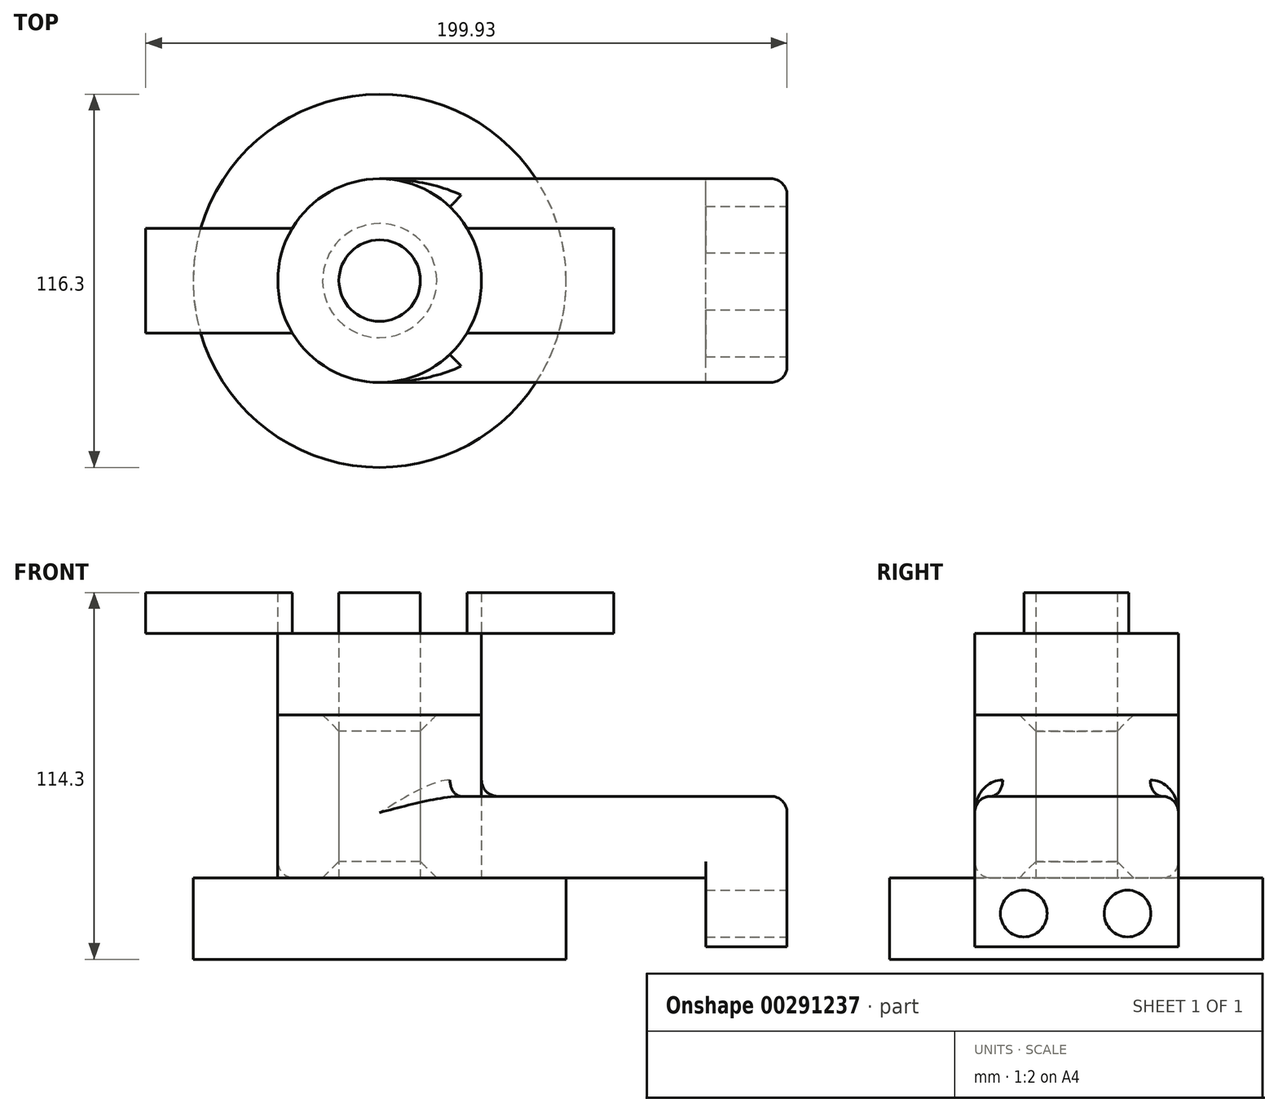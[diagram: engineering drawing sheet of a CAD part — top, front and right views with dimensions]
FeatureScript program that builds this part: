
annotation { "Feature Type Name" : "Feature", "Feature Type Description" : "" }
export const myFeature = defineFeature(function(context is Context, id is Id, definition is map)
    precondition{}
    {
        {
            var Q0;
            Q0=qCreatedBy(makeId("Top.planeOp"),FACE);
            var sketch = newSketch(context, id + "F0", { "sketchPlane" : qUnion([Q0])});
            skLineSegment(sketch, "E0.bottom", {"start": v(0, 0) * mm, "end": v(127, 0) * mm});
            skLineSegment(sketch, "E0.top", {"start": v(0, 63.5) * mm, "end": v(127, 63.5) * mm});
            skLineSegment(sketch, "E0.left", {"start": v(0, 0) * mm, "end": v(0, 63.5) * mm});
            skLineSegment(sketch, "E0.right", {"start": v(127, 0) * mm, "end": v(127, 63.5) * mm});
            skCircle(sketch, "E1", {"center": v(0, 31.75) * mm, "radius": 31.75 * mm});
            skCircle(sketch, "E2", {"center": v(0, 31.75) * mm, "radius": 12.7 * mm});
            skSolve(sketch);
        }
        {
            var Q0;
            {var subQ1=sQuery(id+"F0.wireOp",EDGE,"E0.left");var subQ3=sQuery(id+"F0.wireOp",EDGE,"E2");var subQ4=makeQuery(id+"F0.imprint","INTERSECT",VERTEX,{"disambiguationData":[OD(0.0)],"derivedFrom":[subQ1,subQ3]});Q0=makeQuery(id+"F0.imprint","IMPRINT",FACE,{"disambiguationData":[TD([[makeQuery(id+"F0.imprint","IMPRINT",EDGE,{"disambiguationData":[TD([[subQ4,1.0]])],"derivedFrom":subQ3}),-1.0]])]});}
            var Q1;
            {var subQ1=sQuery(id+"F0.wireOp",EDGE,"E0.left");var subQ3=sQuery(id+"F0.wireOp",EDGE,"E2");var subQ4=makeQuery(id+"F0.imprint","INTERSECT",VERTEX,{"disambiguationData":[OD(0.0)],"derivedFrom":[subQ1,subQ3]});Q1=makeQuery(id+"F0.imprint","IMPRINT",FACE,{"disambiguationData":[TD([[makeQuery(id+"F0.imprint","IMPRINT",EDGE,{"disambiguationData":[TD([[subQ4,-1.0]])],"derivedFrom":subQ3}),-1.0]])]});}
            var Q2;
            {var subQ0=sQuery(id+"F0.wireOp",EDGE,"E0.bottom");Q2=makeQuery(id+"F0.imprint","IMPRINT",FACE,{"disambiguationData":[TD([[makeQuery(id+"F0.imprint","IMPRINT",EDGE,{"derivedFrom":subQ0}),1.0]])]});}
            extrude(context, id + "F1", {"entities" : qUnion([Q0, Q1, Q2]), "depth" : 25.4 * mm});
        }
        {
            var Q0;
            {var subQ1=sQuery(id+"F0.wireOp",EDGE,"E0.left");var subQ3=sQuery(id+"F0.wireOp",EDGE,"E2");var subQ4=makeQuery(id+"F0.imprint","INTERSECT",VERTEX,{"disambiguationData":[OD(0.0)],"derivedFrom":[subQ1,subQ3]});Q0=makeQuery(id+"F0.imprint","IMPRINT",FACE,{"disambiguationData":[TD([[makeQuery(id+"F0.imprint","IMPRINT",EDGE,{"disambiguationData":[TD([[subQ4,1.0]])],"derivedFrom":subQ3}),-1.0]])]});}
            var Q1;
            {var subQ1=sQuery(id+"F0.wireOp",EDGE,"E0.left");var subQ3=sQuery(id+"F0.wireOp",EDGE,"E2");var subQ4=makeQuery(id+"F0.imprint","INTERSECT",VERTEX,{"disambiguationData":[OD(0.0)],"derivedFrom":[subQ1,subQ3]});Q1=makeQuery(id+"F0.imprint","IMPRINT",FACE,{"disambiguationData":[TD([[makeQuery(id+"F0.imprint","IMPRINT",EDGE,{"disambiguationData":[TD([[subQ4,-1.0]])],"derivedFrom":subQ3}),-1.0]])]});}
            extrude(context, id + "F2", {"entities" : qUnion([Q0, Q1]), "operationType" : NewBodyOperationType.ADD, "depth" : 50.8 * mm});
        }
        {
            var Q0;
            Q0=makeQuery(id+"F1.opExtrude","SWEPT_FACE",FACE,{"disambiguationData":[OSD([sQuery(id+"F0.wireOp",EDGE,"E0.right")])]});
            var sketch = newSketch(context, id + "F3", { "sketchPlane" : qUnion([Q0])});
            skLineSegment(sketch, "E3.bottom", {"start": v(0, 0) * mm, "end": v(63.5, 0) * mm});
            skLineSegment(sketch, "E3.top", {"start": v(0, -21.55) * mm, "end": v(63.5, -21.55) * mm});
            skLineSegment(sketch, "E3.left", {"start": v(0, 0) * mm, "end": v(0, -21.55) * mm});
            skLineSegment(sketch, "E3.right", {"start": v(63.5, 0) * mm, "end": v(63.5, -21.55) * mm});
            skSolve(sketch);
        }
        {
            var Q0;
            Q0=makeQuery(id+"F3.imprint","IMPRINT",FACE,{"disambiguationData":[TD([[makeQuery(id+"F3.imprint","IMPRINT",EDGE,{"derivedFrom":sQuery(id+"F3.wireOp",EDGE,"E3.bottom")}),-1.0]])]});
            var sketch = newSketch(context, id + "F4", { "sketchPlane" : qUnion([Q0])});
            skLineSegment(sketch, "E4", {"start": v(31.5, 0) * mm, "end": v(31.5, -22.54) * mm, "construction": true});
            skCircle(sketch, "E5", {"center": v(15.33, -11.15) * mm, "radius": 7.27 * mm});
            skCircle(sketch, "E6.MirrorC", {"center": v(47.68, -11.15) * mm, "radius": 7.27 * mm});
            skSolve(sketch);
        }
        {
            var Q0;
            Q0=makeQuery(id+"F4.imprint","IMPRINT",FACE,{"disambiguationData":[TD([[makeQuery(id+"F4.imprint","IMPRINT",EDGE,{"derivedFrom":sQuery(id+"F4.wireOp",EDGE,"E5")}),-1.0]])]});
            extrude(context, id + "F5", {"entities" : qUnion([Q0]), "operationType" : NewBodyOperationType.ADD, "oppositeDirection" : true, "depth" : 25.4 * mm});
        }
        {
            var Q0;
            {var subQ0=sQuery(id+"F0.wireOp",EDGE,"E1");Q0=makeQuery(id+"F2.boolean.opBoolean","INTERSECT",EDGE,{"derivedFrom":[makeQuery(id+"F1.opExtrude","CAP_FACE",FACE,{"disambiguationData":[OSD([sQuery(id+"F0.wireOp",EDGE,"E0.bottom"),sQuery(id+"F0.wireOp",EDGE,"E0.top"),sQuery(id+"F0.wireOp",EDGE,"E0.right"),subQ0,sQuery(id+"F0.wireOp",EDGE,"E2")])],"isStart":false}),makeQuery(id+"F2.opExtrude","SWEPT_FACE",FACE,{"disambiguationData":[OSD([subQ0])]})]});}
            var Q1;
            Q1=makeQuery(id+"F1.opExtrude","CAP_EDGE",EDGE,{"disambiguationData":[OSD([sQuery(id+"F0.wireOp",EDGE,"E0.bottom")])],"isStart":false});
            var Q2;
            Q2=makeQuery(id+"F1.opExtrude","CAP_EDGE",EDGE,{"disambiguationData":[OSD([sQuery(id+"F0.wireOp",EDGE,"E0.top")])],"isStart":false});
            var Q3;
            Q3=makeQuery(id+"F1.opExtrude","CAP_EDGE",EDGE,{"disambiguationData":[OSD([sQuery(id+"F0.wireOp",EDGE,"E0.right")])],"isStart":false});
            var Q4;
            Q4=makeQuery(id+"F1.opExtrude","CAP_EDGE",EDGE,{"disambiguationData":[OSD([sQuery(id+"F0.wireOp",EDGE,"E0.bottom")])],"isStart":true});
            var Q5;
            Q5=makeQuery(id+"F5.opExtrude","CAP_EDGE",EDGE,{"disambiguationData":[OSD([sQuery(id+"F3.wireOp",EDGE,"E3.bottom")])],"isStart":false});
            fillet(context, id + "F6", {"entities" : qUnion([Q0, Q1, Q2, Q3, Q4, Q5]), "radius" : 5.08 * mm, "tangentPropagation" : true, "allowEdgeOverflow" : false});
        }
        {
            var Q0;
            Q0=makeQuery(id+"F2.opExtrude","CAP_EDGE",EDGE,{"disambiguationData":[OSD([sQuery(id+"F0.wireOp",EDGE,"E2")])],"isStart":false});
            var Q1;
            Q1=makeQuery(id+"F1.opExtrude","CAP_EDGE",EDGE,{"disambiguationData":[OSD([sQuery(id+"F0.wireOp",EDGE,"E2")])],"isStart":true});
            chamfer(context, id + "F7", {"entities" : qUnion([Q0, Q1]), "width" : 5.08 * mm, "tangentPropagation" : true});
        }
        {
            var Q0;
            Q0=makeQuery(id+"F5.boolean.opBoolean","MERGE",EDGE,{"derivedFrom":[makeQuery(id+"F1.opExtrude","SWEPT_EDGE",EDGE,{"disambiguationData":[OSD([sQuery(id+"F0.wireOp",EDGE,"E0.bottom"),sQuery(id+"F0.wireOp",EDGE,"E0.right")])]}),makeQuery(id+"F5.opExtrude","CAP_EDGE",EDGE,{"disambiguationData":[OSD([sQuery(id+"F3.wireOp",EDGE,"E3.left")])],"isStart":true})]});
            var Q1;
            Q1=makeQuery(id+"F5.boolean.opBoolean","MERGE",EDGE,{"derivedFrom":[makeQuery(id+"F1.opExtrude","SWEPT_EDGE",EDGE,{"disambiguationData":[OSD([sQuery(id+"F0.wireOp",EDGE,"E0.top"),sQuery(id+"F0.wireOp",EDGE,"E0.right")])]}),makeQuery(id+"F5.opExtrude","CAP_EDGE",EDGE,{"disambiguationData":[OSD([sQuery(id+"F3.wireOp",EDGE,"E3.right")])],"isStart":true})]});
            fillet(context, id + "F8", {"entities" : qUnion([Q0, Q1]), "radius" : 5.08 * mm, "tangentPropagation" : true, "allowEdgeOverflow" : false});
        }
        {
            var Q0;
            {var subQ0=sQuery(id+"F0.wireOp",EDGE,"E2");var subQ1=sQuery(id+"F0.wireOp",EDGE,"E0.left");var subQ2=makeQuery(id+"F0.imprint","INTERSECT",VERTEX,{"disambiguationData":[OD(0.0)],"derivedFrom":[subQ1,subQ0]});Q0=makeQuery(id+"F0.imprint","IMPRINT",FACE,{"disambiguationData":[TD([[makeQuery(id+"F0.imprint","IMPRINT",EDGE,{"disambiguationData":[TD([[subQ2,-1.0]])],"derivedFrom":subQ1}),1.0]])]});}
            var Q1;
            {var subQ0=sQuery(id+"F0.wireOp",EDGE,"E2");var subQ1=sQuery(id+"F0.wireOp",EDGE,"E0.left");var subQ2=makeQuery(id+"F0.imprint","INTERSECT",VERTEX,{"disambiguationData":[OD(0.0)],"derivedFrom":[subQ1,subQ0]});Q1=makeQuery(id+"F0.imprint","IMPRINT",FACE,{"disambiguationData":[TD([[makeQuery(id+"F0.imprint","IMPRINT",EDGE,{"disambiguationData":[TD([[subQ2,-1.0]])],"derivedFrom":subQ1}),-1.0]])]});}
            extrude(context, id + "F9", {"entities" : qUnion([Q0, Q1]), "depth" : 76.2 * mm});
        }
        {
            var Q0;
            Q0=makeQuery(id+"F9.opExtrude","CAP_FACE",FACE,{"disambiguationData":[OSD([sQuery(id+"F0.wireOp",EDGE,"E2")])],"isStart":false});
            var sketch = newSketch(context, id + "F10", { "sketchPlane" : qUnion([Q0])});
            skLineSegment(sketch, "E7.bottom", {"start": v(72.93, 48.04) * mm, "end": v(-72.93, 48.04) * mm});
            skLineSegment(sketch, "E7.top", {"start": v(72.93, 15.46) * mm, "end": v(-72.93, 15.46) * mm});
            skLineSegment(sketch, "E7.left", {"start": v(72.93, 48.04) * mm, "end": v(72.93, 15.46) * mm});
            skLineSegment(sketch, "E7.right", {"start": v(-72.93, 48.04) * mm, "end": v(-72.93, 15.46) * mm});
            skPoint(sketch, "E7.middle", {"position": v(0, 31.75) * mm});
            skSolve(sketch);
        }
        {
            var Q0;
            Q0=makeQuery(id+"F10.imprint","IMPRINT",FACE,{"disambiguationData":[TD([[makeQuery(id+"F10.imprint","IMPRINT",EDGE,{"derivedFrom":sQuery(id+"F10.wireOp",EDGE,"E7.bottom")}),1.0]])]});
            var Q1;
            Q1=makeQuery(id+"F10.imprint","IMPRINT",FACE,{"disambiguationData":[TD([[makeQuery(id+"F10.imprint","IMPRINT",EDGE,{"derivedFrom":makeQuery(id+"F9.opExtrude","CAP_EDGE",EDGE,{"disambiguationData":[OSD([sQuery(id+"F0.wireOp",EDGE,"E2")])],"isStart":false})}),1.0]])]});
            extrude(context, id + "F11", {"entities" : qUnion([Q0, Q1]), "operationType" : NewBodyOperationType.ADD, "depth" : 12.7 * mm});
        }
        {
            var Q0;
            {var subQ1=sQuery(id+"F0.wireOp",EDGE,"E0.left");var subQ3=sQuery(id+"F0.wireOp",EDGE,"E2");var subQ4=makeQuery(id+"F0.imprint","INTERSECT",VERTEX,{"disambiguationData":[OD(0.0)],"derivedFrom":[subQ1,subQ3]});Q0=makeQuery(id+"F0.imprint","IMPRINT",FACE,{"disambiguationData":[TD([[makeQuery(id+"F0.imprint","IMPRINT",EDGE,{"disambiguationData":[TD([[subQ4,1.0]])],"derivedFrom":subQ3}),-1.0]])]});}
            var sketch = newSketch(context, id + "F12", { "sketchPlane" : qUnion([Q0])});
            skCircle(sketch, "E8", {"center": v(0, 31.7) * mm, "radius": 58.15 * mm});
            skSolve(sketch);
        }
        {
            var Q0;
            Q0 = qSketchRegion(id + "F12", true);
            extrude(context, id + "F13", {"entities" : qUnion([Q0]), "oppositeDirection" : true, "depth" : 25.4 * mm});
        }
    });
